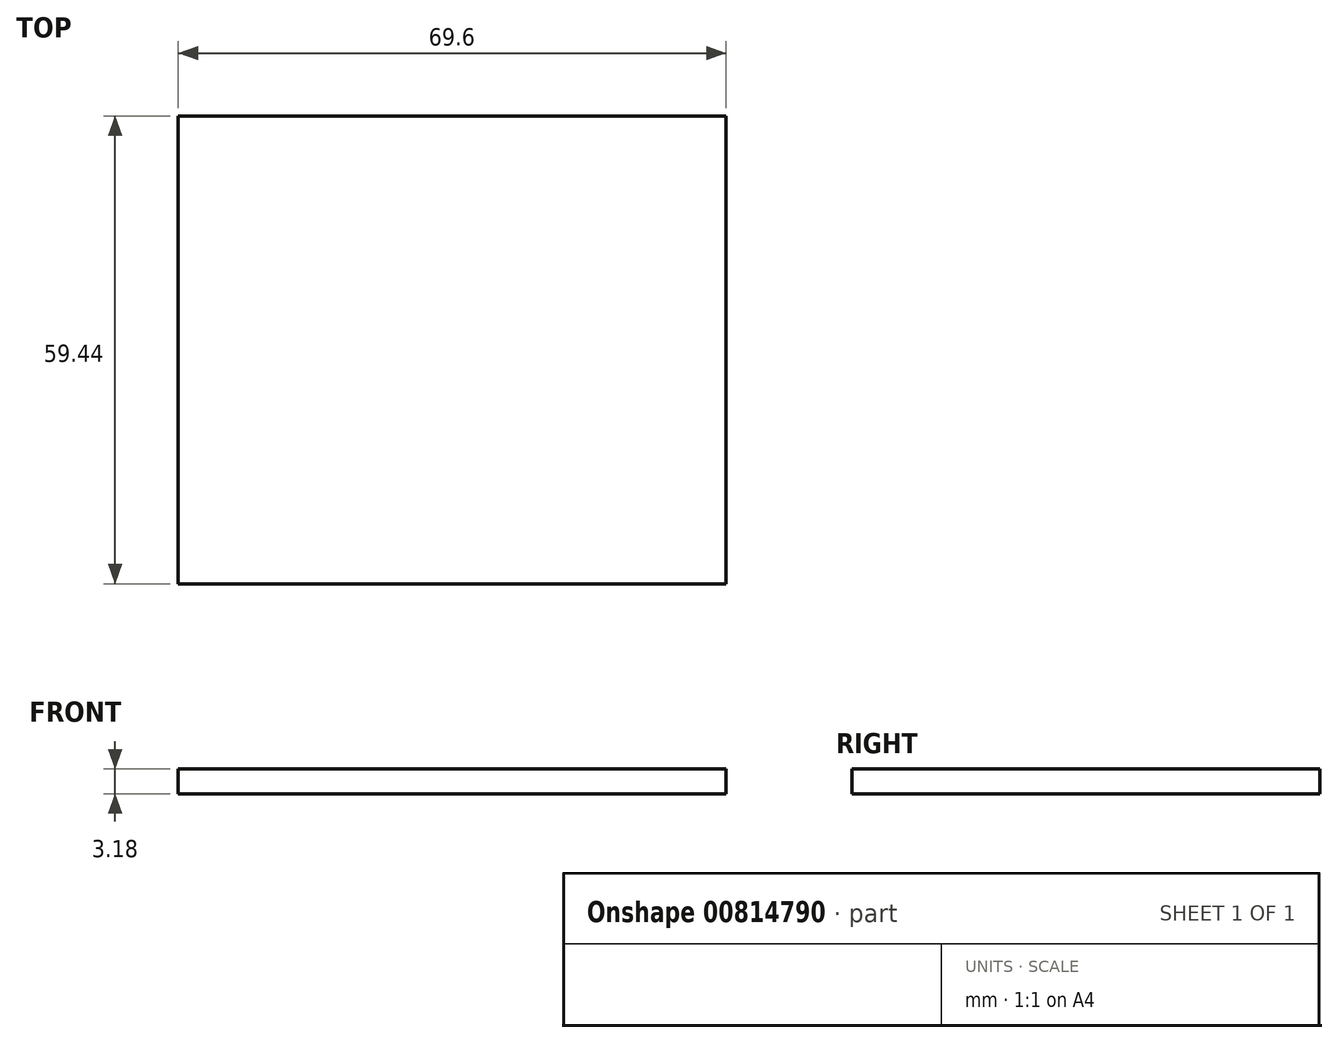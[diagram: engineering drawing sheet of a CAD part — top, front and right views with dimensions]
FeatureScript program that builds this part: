
annotation { "Feature Type Name" : "Feature", "Feature Type Description" : "" }
export const myFeature = defineFeature(function(context is Context, id is Id, definition is map)
    precondition{}
    {
        {
            var Q0;
            Q0=qCreatedBy(makeId("Top.planeOp"),FACE);
            var sketch = newSketch(context, id + "F0", { "sketchPlane" : qUnion([Q0])});
            skLineSegment(sketch, "E0.bottom", {"start": v(34.8, 29.72) * mm, "end": v(-34.8, 29.72) * mm});
            skLineSegment(sketch, "E0.top", {"start": v(34.8, -29.72) * mm, "end": v(-34.8, -29.72) * mm});
            skLineSegment(sketch, "E0.left", {"start": v(34.8, 29.72) * mm, "end": v(34.8, -29.72) * mm});
            skLineSegment(sketch, "E0.right", {"start": v(-34.8, 29.72) * mm, "end": v(-34.8, -29.72) * mm});
            skPoint(sketch, "E0.middle", {"position": v(0, 0) * mm});
            skSolve(sketch);
        }
        {
            var Q0;
            Q0 = qSketchRegion(id + "F0", true);
            extrude(context, id + "F1", {"entities" : qUnion([Q0]), "endBound" : BoundingType.SYMMETRIC, "depth" : 3.17 * mm, "offsetDistance" : 25.4 * mm});
        }
    });
